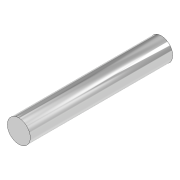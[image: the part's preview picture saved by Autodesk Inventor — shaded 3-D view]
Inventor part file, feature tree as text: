
AUTODESK INVENTOR PART (.ipt)
format: ipt  version: 2020 (Build 240168000, 168)  size: 78,336 bytes
history: native  units: in
note: dims shown in document units (in); Inventor stores cm internally (conversion verified against a paired STEP export)
features: extrude x1, sketch x1
ambient origin geometry x8: Origin, YZ Plane, XZ Plane, XY Plane, X Axis, Y Axis, Z Axis, Center Point
bodies: Solid1 (feature_tree)
feature tree (2):
  extrude  "Extrusion1"  Depth=1.2205in TaperAngle=0.0deg
  sketch  "Sketch1"  dims[d0=0.1969in d1=1.2205in d2=0.0in]
